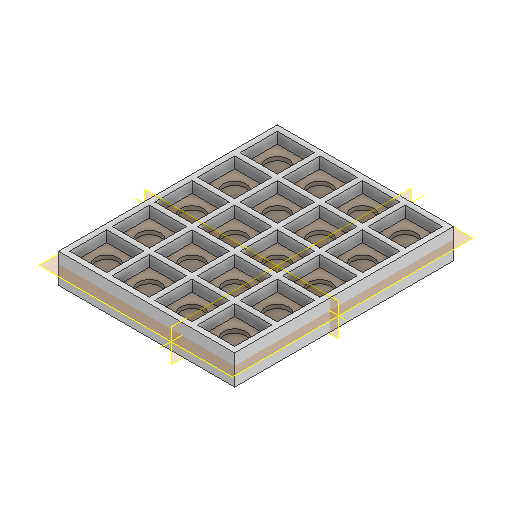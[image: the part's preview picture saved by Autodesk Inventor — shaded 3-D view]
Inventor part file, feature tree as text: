
AUTODESK INVENTOR PART (.ipt)
format: ipt  version: 2025.1 (Build 291241000, 241)  size: 306,176 bytes
history: native  units: mm
features: sketch x6, extrude x3
ambient origin geometry x8: Origin, YZ Plane, XZ Plane, XY Plane, X Axis, Y Axis, Z Axis, Center Point
bodies: Solid1 (feature_tree)
feature tree (9):
  extrude  "Extrusion1"  Depth=47.5mm
  extrude  "Extrusion2"  Depth=1.5mm
  extrude  "Extrusion3"  Depth=10.0mm
  sketch  "Sketch1"  dims[d0=59.0mm d1=47.5mm]
  sketch  "Sketch2"  dims[d5=1.5mm d6=10.0mm]
  sketch  "Sketch Rectangular Pattern1"  dims[d2=5.0mm d3=0.0mm d4=1.5mm]
  sketch  "Sketch Rectangular Pattern2"  dims[d7=50.0mm d9=11.5mm d10=10.0mm d12=10.0mm]
  sketch  "Sketch3"  dims[d14=50.0mm d16=11.5mm d17=10.0mm d19=10.0mm]
  sketch  "Sketch Rectangular Pattern3"  dims[d21=3.0mm d22=0.0mm d23=6.0mm d24=5.0mm d25=5.0mm d26=40.0mm d28=11.5mm d29=50.0mm d31=11.5mm d34=1.0mm d35=0.0mm]
